# Revit family: MusicLibrarySystem_Wenger_6-Shelf_Single
name_source: partatom
category: Furniture
revit_build: Autodesk Revit 2015 (Build: 20140606_1530(x64)
units: mm (PartAtom-declared; Revit-internal decimal feet)

## types (2) — shared parameters
Assembly Code = E2010200
Construction Details = http://www.arcat.com
Depth = 3' - 7 1/4"
Edge Banding Finish = Wenger Cherry (Use Cherry Edge Band Only)
Floor Offset = 0' - 0 1/8"
Frame Finish = Metal - White Powdercoat
Frame LH = Yes
Frame RH = Yes
Green Building-LEED = http://www.arcat.com
Hardware Finish = Metal - White Powdercoat
Height = 6' - 9 1/2"
Height to Bottom Shelf = 0' - 8"
Keynote = 12 35 83
Manufacturer = Wenger Corporation
Manufacturer Fax = (507) 455-4258
Manufacturer Website = https://www.wengercorp.com
Panel Thickness = 0' - 0 3/4"
Product Data = http://www.arcat.com
Revision = R1_2018-04
Sales Information = https://www.wengercorp.com
Shelf Depth = 2' - 10 1/2"
Shelf Finish = Wenger Oyster (Use Oyster Edge Band Only)
Specification = http://www.arcat.com
Tubular Frame Width = 0' - 1 1/2"
URL = https://www.wengercorp.com
zero-valued in all types: Cost

## per-type parameters (varying)
| type | Description | Model | Overall Width | Type Comments |
| Oversized | Wenger 6 Shelf Oversized Music Library System | 6 Shelf Oversized | 1' - 10" | 6 Shelf, Oversized, 1 Unit |
| UltraStor | Wenger 6 Shelf Standard Music Library System | 6 Shelf Standard | 1' - 7" | 6 Shelf, Standard, 1 Unit |

## geometry (parser evidence)
native form markers: Blend x10, Sweep x4
no freeform markers — native parametric forms only
